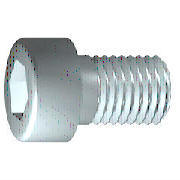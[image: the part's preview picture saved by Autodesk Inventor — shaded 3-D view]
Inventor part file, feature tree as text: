
AUTODESK INVENTOR PART (.ipt)
format: ipt  version: 2011 (Build 150239000, 239)  size: 180,224 bytes
history: native  units: mm (DEFAULTED — no unit token found)
features: extrude x1, plane x1
ambient origin geometry x7: Origin, YZ Plane, XY Plane, X Axis, Y Axis, Z Axis, Center Point
bodies: Solid1 (feature_tree), Body (feature_tree)
feature tree (2):
  extrude  "Slot"  Depth=31.75mm
  plane  "Work Plane1"
